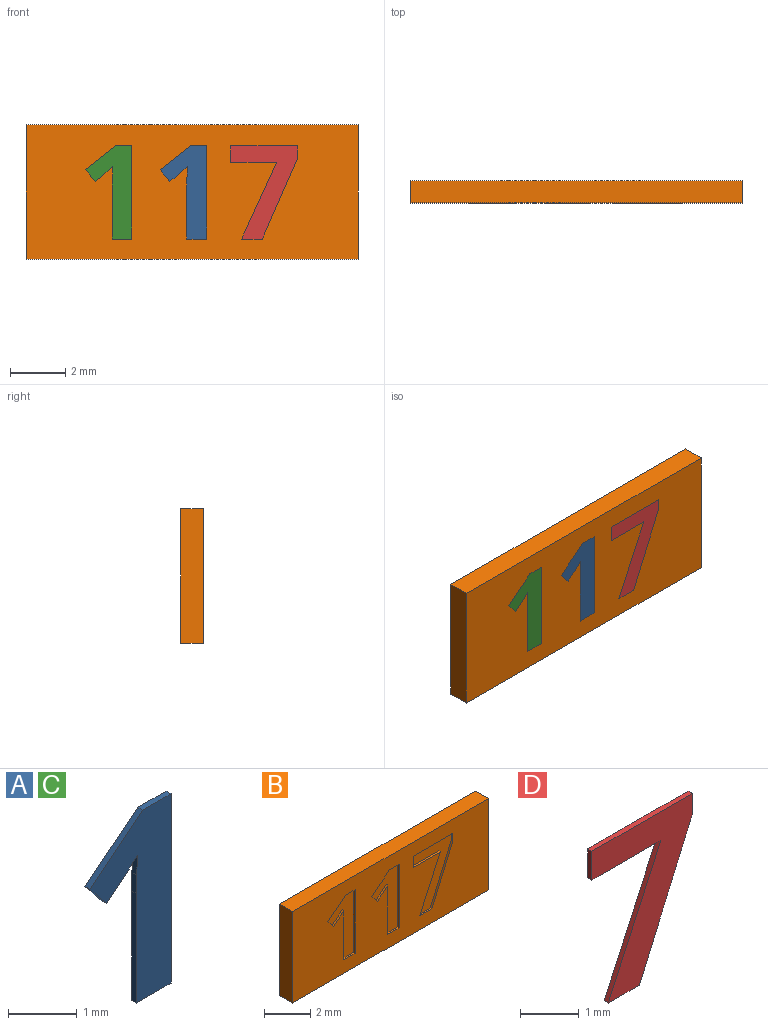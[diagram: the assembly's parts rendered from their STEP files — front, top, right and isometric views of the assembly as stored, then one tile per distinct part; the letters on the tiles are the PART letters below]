
ASSEMBLY  parts=4 mates=3
PART A: 12 faces, bbox 1.7x0.1x3.4 mm
  f0: plane 3.37x1.67mm, normal (0,-1,0), area 2.9mm2, adj f1,f2,f3,f4,f5,f6,f7,f9
  f1: plane 0.59x0.1mm, normal (0,0,1), area 0.1mm2, adj f0,f2,f8,f10
  f2: plane 1.09x0.86mm, normal (-0.62,0,0.78), area 0.1mm2, adj f0,f1,f3,f8
  f3: plane 0.43x0.34mm, normal (-0.78,0,-0.63), area 0.1mm2, adj f0,f2,f4,f8
  f4: plane 0.39x0.31mm, normal (0.63,0,-0.78), area 0mm2, adj f0,f3,f5,f8
  f5: extruded ~0.25x0.23mm, area 0mm2, adj f0,f4,f6,f8
  f6: plane 0.35x0.1mm, normal (-1,0,0.03), area 0mm2, adj f0,f5,f7,f8
  f7: plane 0.32x0.1mm, normal (-1,0,0.02), area 0mm2, adj f0,f6,f8,f9
  f8: plane 3.37x1.67mm, normal (0,1,0), area 2.9mm2, adj f1,f2,f3,f4,f5,f6,f7,f9
  f9: plane 1.95x0.1mm, normal (-1,0,0), area 0.2mm2, adj f0,f7,f8,f11
  f10: plane 3.37x0.1mm, normal (1,0,0), area 0.3mm2, adj f0,f1,f8,f11
  f11: plane 0.71x0.1mm, normal (0,0,-1), area 0.1mm2, adj f0,f8,f9,f10
PART B: 36 faces, bbox 12x0.8x4.9 mm
  f0: plane 12x4.85mm, normal (0,-1,0), area 48.9mm2, adj f1,f2,f3,f4,f6,f7,f8,f9
  f1: plane 12x0.8mm, normal (0,0,-1), area 9.6mm2, adj f0,f2,f4,f5
  f2: plane 4.85x0.8mm, normal (1,0,0), area 3.9mm2, adj f0,f1,f3,f5
  f3: plane 12x0.8mm, normal (0,0,1), area 9.6mm2, adj f0,f2,f4,f5
  f4: plane 4.85x0.8mm, normal (-1,0,0), area 3.9mm2, adj f0,f1,f3,f5
  f5: plane 12x4.85mm, normal (0,1,0), area 58.2mm2, adj f1,f2,f3,f4
  f6: plane 0.75x0.1mm, normal (0,0,1), area 0.1mm2, adj f0,f7,f12,f13
  f7: plane 2.92x1.28mm, normal (-0.92,0,0.4), area 0.3mm2, adj f0,f6,f8,f13
  f8: plane 0.45x0.1mm, normal (-1,0,0), area 0mm2, adj f0,f7,f9,f13
  f9: plane 2.42x0.1mm, normal (0,0,-1), area 0.2mm2, adj f0,f8,f10,f13
  f10: plane 0.6x0.1mm, normal (1,0,0), area 0.1mm2, adj f0,f9,f11,f13
  f11: plane 1.66x0.1mm, normal (0,0,1), area 0.2mm2, adj f0,f10,f12,f13
  f12: plane 2.77x1.27mm, normal (0.91,0,-0.42), area 0.3mm2, adj f0,f6,f11,f13
  f13: plane 3.37x2.42mm, normal (0,-1,0), area 3.4mm2, adj f6,f7,f8,f9,f10,f11,f12
  f14: plane 3.37x0.1mm, normal (-1,0,0), area 0.3mm2, adj f0,f15,f23,f24
  f15: plane 0.59x0.1mm, normal (0,0,-1), area 0.1mm2, adj f0,f14,f16,f24
  f16: plane 1.09x0.86mm, normal (0.62,0,-0.78), area 0.1mm2, adj f0,f15,f17,f24
  f17: plane 0.43x0.34mm, normal (0.78,0,0.63), area 0.1mm2, adj f0,f16,f18,f24
  f18: plane 0.39x0.31mm, normal (-0.63,0,0.78), area 0mm2, adj f0,f17,f19,f24
  f19: extruded ~0.25x0.23mm, area 0mm2, adj f0,f18,f20,f24
  f20: plane 0.35x0.1mm, normal (1,0,-0.03), area 0mm2, adj f0,f19,f21,f24
  f21: plane 0.32x0.1mm, normal (1,0,-0.02), area 0mm2, adj f0,f20,f22,f24
  f22: plane 1.95x0.1mm, normal (1,0,0), area 0.2mm2, adj f0,f21,f23,f24
  f23: plane 0.71x0.1mm, normal (0,0,1), area 0.1mm2, adj f0,f14,f22,f24
  f24: plane 3.37x1.67mm, normal (0,-1,0), area 2.9mm2, adj f14,f15,f16,f17,f18,f19,f20,f21
  f25: plane 3.37x0.1mm, normal (-1,0,0), area 0.3mm2, adj f0,f26,f34,f35
  f26: plane 0.59x0.1mm, normal (0,0,-1), area 0.1mm2, adj f0,f25,f27,f35
  f27: plane 1.09x0.86mm, normal (0.62,0,-0.78), area 0.1mm2, adj f0,f26,f28,f35
  f28: plane 0.43x0.34mm, normal (0.78,0,0.63), area 0.1mm2, adj f0,f27,f29,f35
  f29: plane 0.39x0.31mm, normal (-0.63,0,0.78), area 0mm2, adj f0,f28,f30,f35
  f30: extruded ~0.25x0.23mm, area 0mm2, adj f0,f29,f31,f35
  f31: plane 0.35x0.1mm, normal (1,0,-0.03), area 0mm2, adj f0,f30,f32,f35
  f32: plane 0.32x0.1mm, normal (1,0,-0.02), area 0mm2, adj f0,f31,f33,f35
  f33: plane 1.95x0.1mm, normal (1,0,0), area 0.2mm2, adj f0,f32,f34,f35
  f34: plane 0.71x0.1mm, normal (0,0,1), area 0.1mm2, adj f0,f25,f33,f35
  f35: plane 3.37x1.67mm, normal (0,-1,0), area 2.9mm2, adj f25,f26,f27,f28,f29,f30,f31,f32
PART C: same geometry as A
PART D: 9 faces, bbox 2.4x0.1x3.4 mm
  f0: plane 3.37x2.42mm, normal (0,-1,0), area 3.4mm2, adj f1,f2,f3,f4,f6,f7,f8
  f1: plane 2.92x1.28mm, normal (0.92,0,-0.4), area 0.3mm2, adj f0,f2,f5,f7
  f2: plane 0.45x0.1mm, normal (1,0,0), area 0mm2, adj f0,f1,f3,f5
  f3: plane 2.42x0.1mm, normal (0,0,1), area 0.2mm2, adj f0,f2,f4,f5
  f4: plane 0.6x0.1mm, normal (-1,0,0), area 0.1mm2, adj f0,f3,f5,f6
  f5: plane 3.37x2.42mm, normal (0,1,0), area 3.4mm2, adj f1,f2,f3,f4,f6,f7,f8
  f6: plane 1.66x0.1mm, normal (0,0,-1), area 0.2mm2, adj f0,f4,f5,f8
  f7: plane 0.75x0.1mm, normal (0,0,-1), area 0.1mm2, adj f0,f1,f5,f8
  f8: plane 2.77x1.27mm, normal (-0.91,0,0.42), area 0.3mm2, adj f0,f5,f6,f7
PLACE A t=(-1.83,0.42,0)mm
PLACE B t=(0.03,0.42,0)mm
PLACE C t=(-4.53,0.42,0)mm
PLACE D t=(1.16,0.42,0)mm
MATE fastened C.f0 <-> B.f0  axis (0,-1,0) through (-2.85,-0.38,-1.7)mm
MATE fastened D.f0 <-> B.f0  axis (0,-1,0) through (1.83,-0.38,-1.7)mm
MATE fastened A.f0 <-> B.f0  axis (0,-1,0) through (-0.15,-0.38,-1.7)mm
